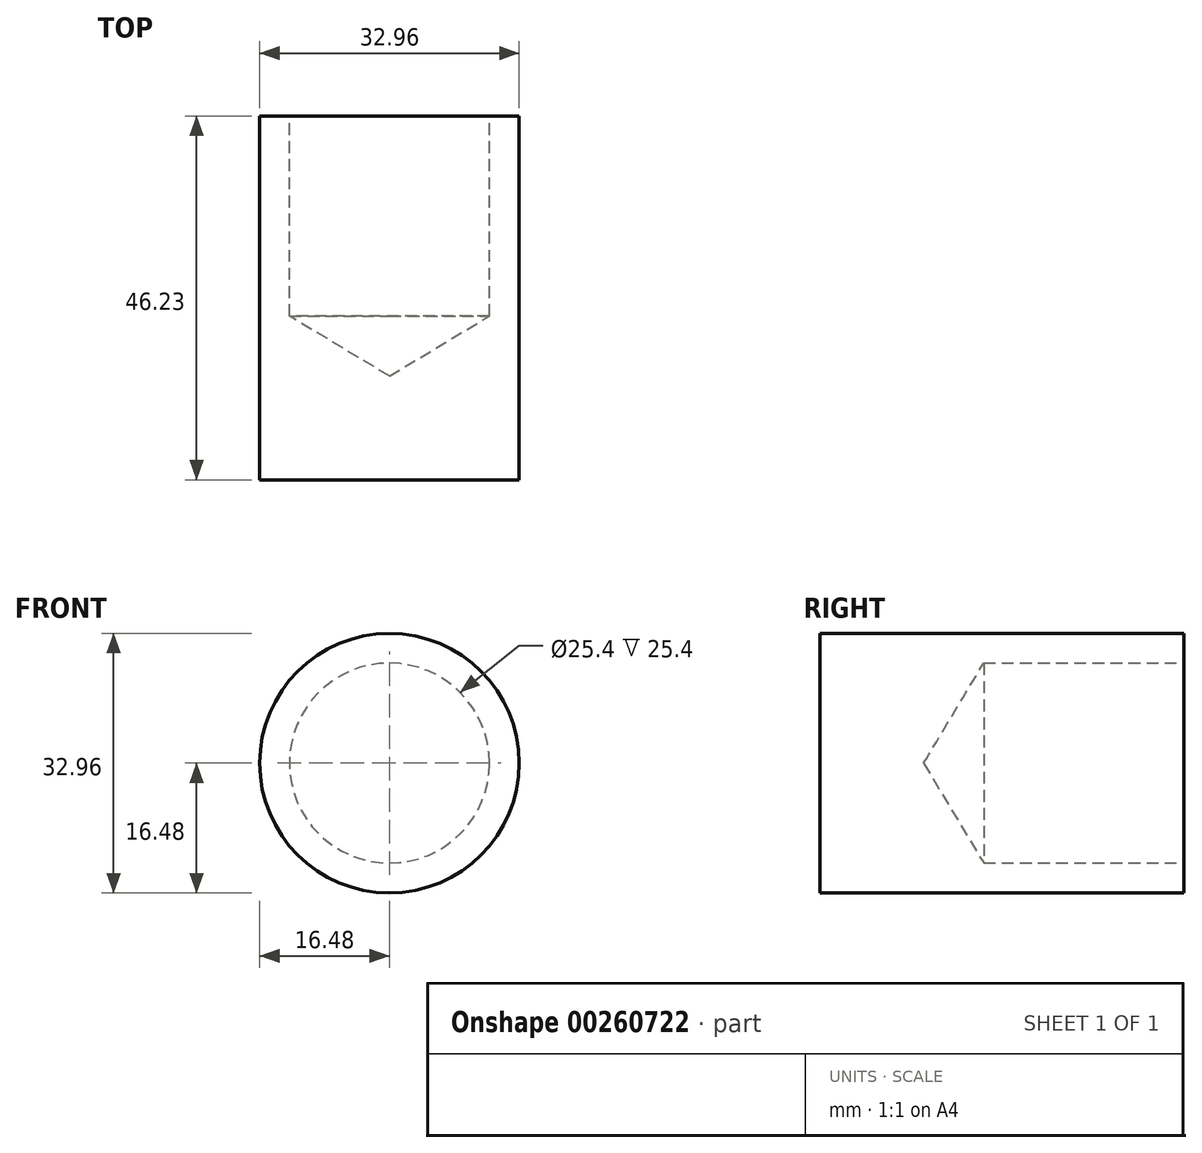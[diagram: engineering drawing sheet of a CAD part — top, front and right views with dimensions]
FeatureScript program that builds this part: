
annotation { "Feature Type Name" : "Feature", "Feature Type Description" : "" }
export const myFeature = defineFeature(function(context is Context, id is Id, definition is map)
    precondition{}
    {
        {
            var Q0;
            Q0=qCreatedBy(makeId("Front.planeOp"),FACE);
            var sketch = newSketch(context, id + "F0", { "sketchPlane" : qUnion([Q0])});
            skCircle(sketch, "E0", {"center": v(0, 0) * mm, "radius": 16.48 * mm});
            skSolve(sketch);
        }
        {
            var Q0;
            Q0 = qSketchRegion(id + "F0", true);
            extrude(context, id + "F1", {"entities" : qUnion([Q0]), "depth" : 46.23 * mm});
        }
        {
            var Q0;
            Q0=qCreatedBy(makeId("Front.planeOp"),FACE);
            var sketch = newSketch(context, id + "F2", { "sketchPlane" : qUnion([Q0])});
            skLineSegment(sketch, "E1.bottom", {"start": v(0, 0) * mm, "end": v(23.9, 0) * mm});
            skLineSegment(sketch, "E1.top", {"start": v(0, -26.43) * mm, "end": v(23.9, -26.43) * mm});
            skLineSegment(sketch, "E1.left", {"start": v(0, 0) * mm, "end": v(0, -26.43) * mm});
            skLineSegment(sketch, "E1.right", {"start": v(23.9, 0) * mm, "end": v(23.9, -26.43) * mm});
            skSolve(sketch);
        }
        {
            var Q0;
            Q0=sQuery(id+"F2.wireOp",VERTEX,"E1.left.start");
            var Q1;
            Q1=makeQuery(id+"F1.opExtrude","SWEPT_BODY",BODY,{"disambiguationData":[OSD([sQuery(id+"F0.wireOp",EDGE,"E0")])]});
            hole(context, id + "F3", {"style" : HoleStyle.SIMPLE, "endStyle" : HoleEndStyle.BLIND, "oppositeDirection" : true, "holeDiameter" : 25.4 * mm, "holeDepth" : 25.4 * mm, "tappedDepth" : 12.7 * mm, "tapClearance" : 3, "locations" : qUnion([Q0]), "scope" : qUnion([Q1])});
        }
    });
